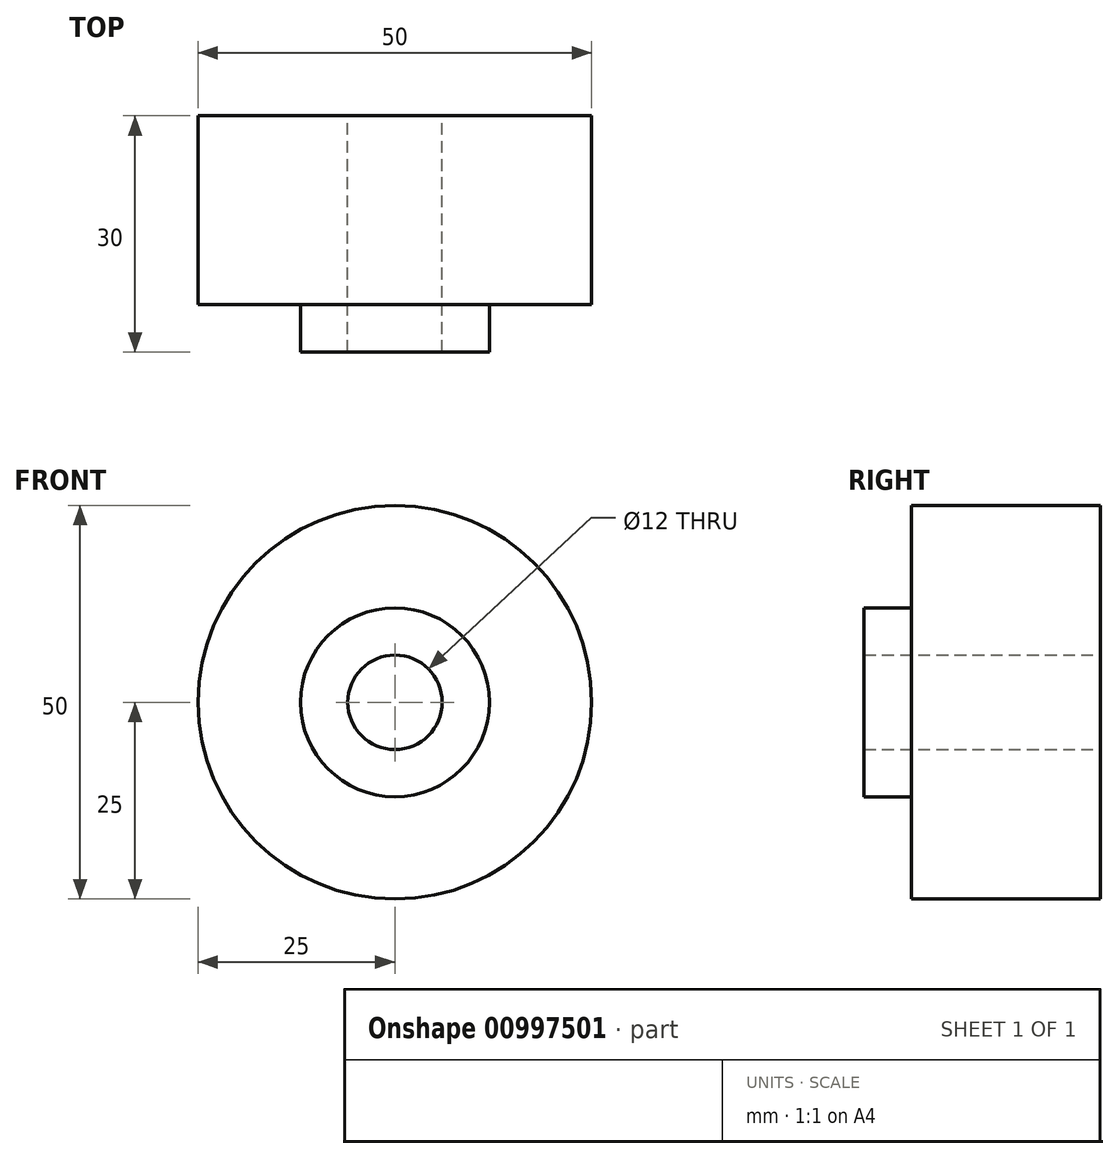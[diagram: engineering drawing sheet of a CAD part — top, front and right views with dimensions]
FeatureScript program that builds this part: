
annotation { "Feature Type Name" : "Feature", "Feature Type Description" : "" }
export const myFeature = defineFeature(function(context is Context, id is Id, definition is map)
    precondition{}
    {
        {
            var Q0;
            Q0=qCreatedBy(makeId("Front.planeOp"),FACE);
            var sketch = newSketch(context, id + "F0", { "sketchPlane" : qUnion([Q0])});
            skCircle(sketch, "E0", {"center": v(0, 0) * mm, "radius": 25 * mm});
            skSolve(sketch);
        }
        {
            var Q0;
            Q0=makeQuery(id+"F0.imprint","IMPRINT",FACE,{"disambiguationData":[TD([[makeQuery(id+"F0.imprint","IMPRINT",EDGE,{"derivedFrom":sQuery(id+"F0.wireOp",EDGE,"E0")}),1.0]])]});
            extrude(context, id + "F1", {"entities" : qUnion([Q0]), "depth" : 24 * mm, "offsetDistance" : 25 * mm});
        }
        {
            var Q0;
            Q0=makeQuery(id+"F1.opExtrude","CAP_FACE",FACE,{"disambiguationData":[OSD([sQuery(id+"F0.wireOp",EDGE,"E0")])],"isStart":false});
            var sketch = newSketch(context, id + "F2", { "sketchPlane" : qUnion([Q0])});
            skCircle(sketch, "E1", {"center": v(0, 0) * mm, "radius": 12 * mm});
            skSolve(sketch);
        }
        {
            var Q0;
            Q0=makeQuery(id+"F2.imprint","IMPRINT",FACE,{"disambiguationData":[TD([[makeQuery(id+"F2.imprint","IMPRINT",EDGE,{"derivedFrom":sQuery(id+"F2.wireOp",EDGE,"E1")}),1.0]])]});
            extrude(context, id + "F3", {"entities" : qUnion([Q0]), "operationType" : NewBodyOperationType.ADD, "depth" : 6 * mm, "offsetDistance" : 25 * mm});
        }
        {
            var Q0;
            Q0=makeQuery(id+"F1.opExtrude","CAP_FACE",FACE,{"disambiguationData":[OSD([sQuery(id+"F0.wireOp",EDGE,"E0")])],"isStart":true});
            var sketch = newSketch(context, id + "F4", { "sketchPlane" : qUnion([Q0])});
            skCircle(sketch, "E2", {"center": v(0, 0) * mm, "radius": 6 * mm});
            skSolve(sketch);
        }
        {
            var Q0;
            Q0=makeQuery(id+"F4.imprint","IMPRINT",FACE,{"disambiguationData":[TD([[makeQuery(id+"F4.imprint","IMPRINT",EDGE,{"derivedFrom":sQuery(id+"F4.wireOp",EDGE,"E2")}),1.0]])]});
            extrude(context, id + "F5", {"entities" : qUnion([Q0]), "operationType" : NewBodyOperationType.REMOVE, "endBound" : BoundingType.THROUGH_ALL, "oppositeDirection" : true, "depth" : 25 * mm, "offsetDistance" : 25 * mm});
        }
    });
